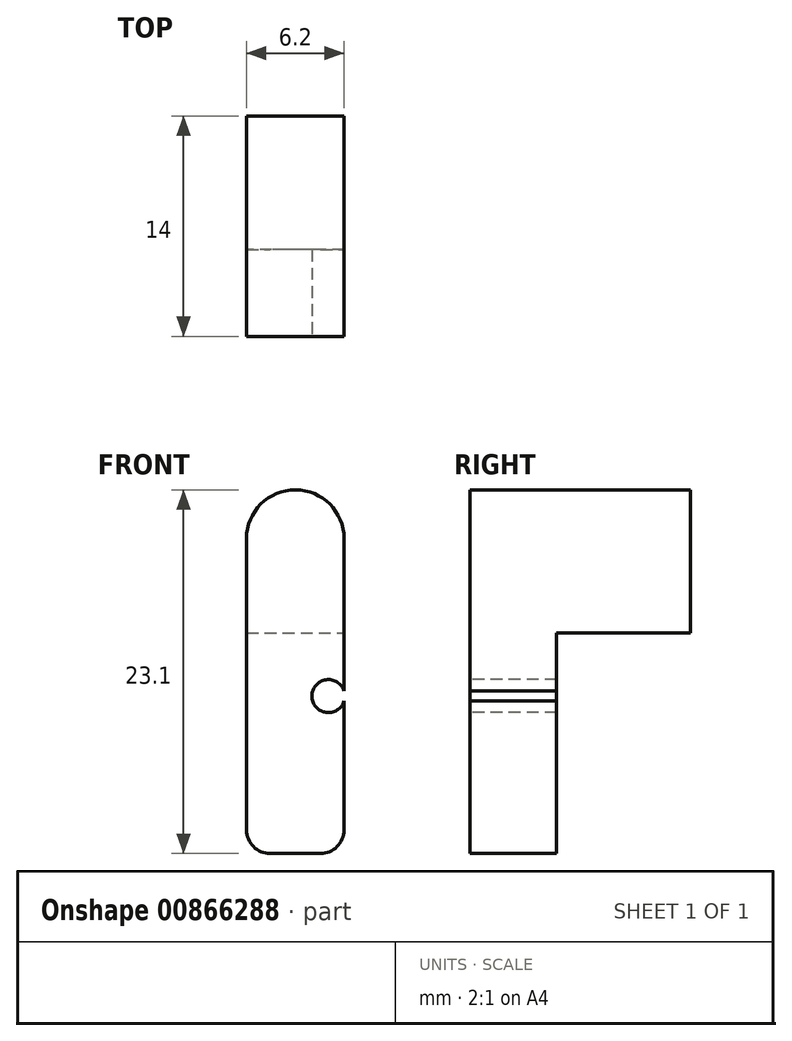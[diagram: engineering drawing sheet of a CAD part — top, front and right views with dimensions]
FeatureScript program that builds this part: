
annotation { "Feature Type Name" : "Feature", "Feature Type Description" : "" }
export const myFeature = defineFeature(function(context is Context, id is Id, definition is map)
    precondition{}
    {
        {
            var Q0;
            Q0=qCreatedBy(makeId("Front.planeOp"),FACE);
            var sketch = newSketch(context, id + "F0", { "sketchPlane" : qUnion([Q0])});
            skArc(sketch, "E0", {"start": v(3.1, 0) * mm, "mid": v(0, 3.1) * mm, "end": v(-3.1, 0) * mm});
            skPoint(sketch, "E1", {"position": v(-3.1, 0) * mm});
            skPoint(sketch, "E2", {"position": v(3.1, 0) * mm});
            skLineSegment(sketch, "E3.top", {"start": v(-3.1, -20) * mm, "end": v(3.1, -20) * mm});
            skLineSegment(sketch, "E3.left", {"start": v(-3.1, 0) * mm, "end": v(-3.1, -20) * mm});
            skLineSegment(sketch, "E3.right", {"start": v(3.1, 0) * mm, "end": v(3.1, -20) * mm});
            skPoint(sketch, "E4.visualSharp", {"position": v(-3.1, -20) * mm});
            skPoint(sketch, "E5.visualSharp", {"position": v(3.1, -20) * mm});
            skSolve(sketch);
        }
        {
            var Q0;
            Q0=makeQuery(id+"F0.imprint","IMPRINT",FACE,{"disambiguationData":[TD([[makeQuery(id+"F0.imprint","IMPRINT",EDGE,{"derivedFrom":sQuery(id+"F0.wireOp",EDGE,"E0")}),1.0]])]});
            extrude(context, id + "F1", {"entities" : qUnion([Q0]), "oppositeDirection" : true, "depth" : 14 * mm, "offsetDistance" : 25 * mm});
        }
        {
            var Q0;
            Q0=makeQuery(id+"F1.opExtrude","SWEPT_FACE",FACE,{"disambiguationData":[OSD([sQuery(id+"F0.wireOp",EDGE,"E3.top")])]});
            var sketch = newSketch(context, id + "F2", { "sketchPlane" : qUnion([Q0])});
            skLineSegment(sketch, "E6.bottom", {"start": v(3.1, -14) * mm, "end": v(-3.1, -14) * mm});
            skLineSegment(sketch, "E6.top", {"start": v(3.1, -5.5) * mm, "end": v(-3.1, -5.5) * mm});
            skLineSegment(sketch, "E6.left", {"start": v(3.1, -14) * mm, "end": v(3.1, -5.5) * mm});
            skLineSegment(sketch, "E6.right", {"start": v(-3.1, -14) * mm, "end": v(-3.1, -5.5) * mm});
            skSolve(sketch);
        }
        {
            var Q0;
            Q0=makeQuery(id+"F2.imprint","IMPRINT",FACE,{"disambiguationData":[TD([[makeQuery(id+"F2.imprint","IMPRINT",EDGE,{"derivedFrom":sQuery(id+"F2.wireOp",EDGE,"E6.bottom")}),1.0]])]});
            extrude(context, id + "F3", {"entities" : qUnion([Q0]), "operationType" : NewBodyOperationType.REMOVE, "oppositeDirection" : true, "depth" : 14 * mm, "offsetDistance" : 25 * mm});
        }
        {
            var Q0;
            Q0=makeQuery(id+"F1.opExtrude","CAP_FACE",FACE,{"disambiguationData":[OSD([sQuery(id+"F0.wireOp",EDGE,"E0"),sQuery(id+"F0.wireOp",EDGE,"E3.top"),sQuery(id+"F0.wireOp",EDGE,"E3.left"),sQuery(id+"F0.wireOp",EDGE,"E3.right")])],"isStart":true});
            cPlane(context, id + "F4", {"entities" : qUnion([Q0]), "cplaneType" : CPlaneType.OFFSET, "offset" : 5 * mm, "width" : 150 * mm, "height" : 150 * mm});
        }
        {
            var Q0;
            Q0=qCreatedBy(id+"F4.planeOp",FACE);
            var sketch = newSketch(context, id + "F5", { "sketchPlane" : qUnion([Q0])});
            skPoint(sketch, "E7", {"position": v(2.1, -10) * mm});
            skSolve(sketch);
        }
        {
            var Q0;
            Q0=sQuery(id+"F5.wireOp",VERTEX,"E7");
            var Q1;
            Q1=makeQuery(id+"F1.opExtrude","SWEPT_BODY",BODY,{"disambiguationData":[OSD([sQuery(id+"F0.wireOp",EDGE,"E0"),sQuery(id+"F0.wireOp",EDGE,"E3.top"),sQuery(id+"F0.wireOp",EDGE,"E3.left"),sQuery(id+"F0.wireOp",EDGE,"E3.right")])]});
            hole(context, id + "F6", {"style" : HoleStyle.SIMPLE, "endStyle" : HoleEndStyle.THROUGH, "holeDiameter" : 2.1 * mm, "majorDiameter" : 5 * mm, "isTappedThrough" : true, "tappedDepth" : 12 * mm, "tapClearance" : 3, "locations" : qUnion([Q0]), "scope" : qUnion([Q1])});
        }
        {
            var Q0;
            Q0=makeQuery(id+"F1.opExtrude","SWEPT_EDGE",EDGE,{"disambiguationData":[OSD([sQuery(id+"F0.wireOp",EDGE,"E3.top"),sQuery(id+"F0.wireOp",EDGE,"E3.right")])]});
            var Q1;
            Q1=makeQuery(id+"F1.opExtrude","SWEPT_EDGE",EDGE,{"disambiguationData":[OSD([sQuery(id+"F0.wireOp",EDGE,"E3.top"),sQuery(id+"F0.wireOp",EDGE,"E3.left")])]});
            fillet(context, id + "F7", {"entities" : qUnion([Q0, Q1]), "radius" : 1.5 * mm, "tangentPropagation" : true, "allowEdgeOverflow" : false});
        }
    });
